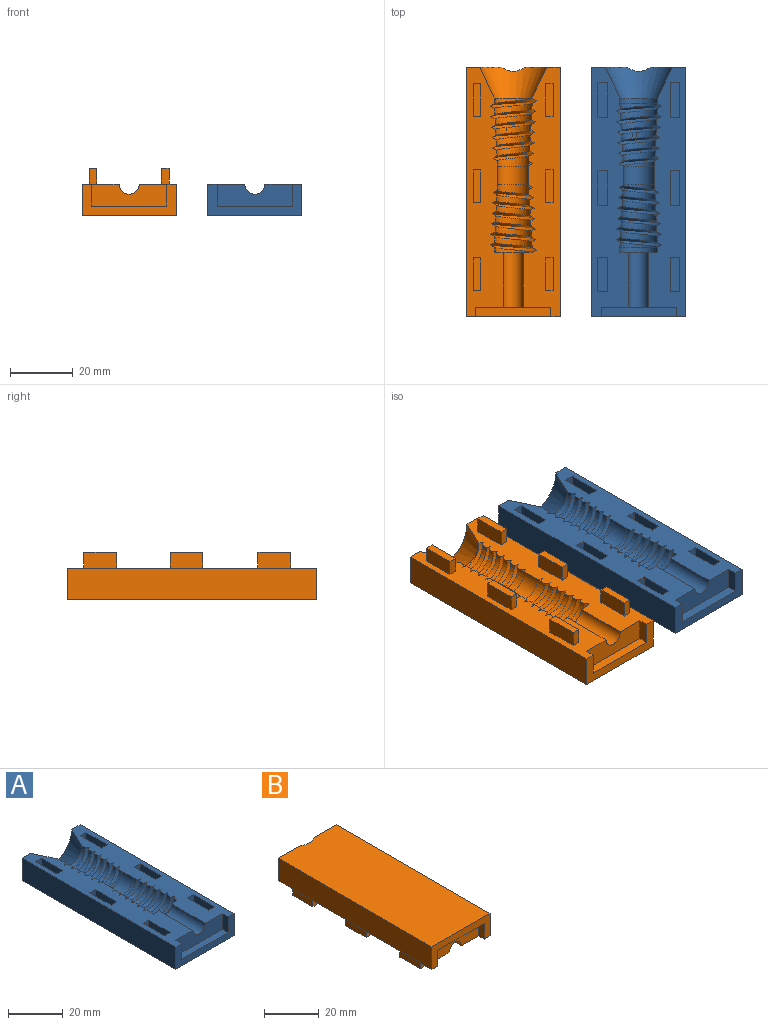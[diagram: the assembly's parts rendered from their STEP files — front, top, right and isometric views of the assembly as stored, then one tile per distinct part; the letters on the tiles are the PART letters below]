
ASSEMBLY  parts=2 mates=3
PART A: 86 faces, bbox 33x82.5x17.5 mm
  f0: plane 79.5x11.8mm, normal (0,0,1), area 638.4mm2, adj f3,f4,f5,f6,f7,f8,f9,f10
  f1: plane 24x3mm, normal (0,0,1), area 72mm2, adj f47,f48,f49,f52
  f2: plane 82.5x32.99mm, normal (0,0,-1), area 2378.5mm2, adj f3,f47,f50,f51,f53,f54
  f3: cone r=5.97mm half-angle=25deg, axis (0,1,0), area 284.2mm2, adj f0,f2,f26,f53,f54,f55
  f4: bspline ~12.74x10mm, area 25.5mm2, adj f0,f5,f21,f26
  f5: bspline ~12.74x10mm, area 26.9mm2, adj f0,f4,f22,f26
  f6: bspline ~13.19x9.88mm, area 26.3mm2, adj f0,f7,f20,f26
  f7: bspline ~13.19x9.88mm, area 27.7mm2, adj f0,f6,f21,f26
  f8: bspline ~13.54x10.18mm, area 27mm2, adj f0,f9,f19,f26
  f9: bspline ~13.54x10.18mm, area 28.5mm2, adj f0,f8,f20,f26
  f10: bspline ~13.83x10.84mm, area 27.8mm2, adj f0,f11,f18,f26
  f11: bspline ~13.83x10.84mm, area 29.4mm2, adj f0,f10,f19,f26
  f12: bspline ~14.2x9.54mm, area 28.6mm2, adj f0,f13,f17,f26
  f13: bspline ~14.2x9.54mm, area 30.2mm2, adj f0,f12,f18,f26
  f14: bspline ~14.59x9.33mm, area 29.4mm2, adj f0,f15,f16,f26
  f15: bspline ~14.59x9.33mm, area 31mm2, adj f0,f14,f17,f26
  f16: cone r=5mm half-angle=3deg, axis (0,1,0), area 19.8mm2, adj f0,f14,f26,f55
  f17: cone r=5mm half-angle=3deg, axis (0,1,0), area 34.7mm2, adj f0,f12,f15,f26
  f18: cone r=5mm half-angle=3deg, axis (0,1,0), area 33.6mm2, adj f0,f10,f13,f26
  f19: cone r=5mm half-angle=3deg, axis (0,1,0), area 32.6mm2, adj f0,f8,f11,f26
  f20: cone r=5mm half-angle=3deg, axis (0,1,0), area 31.6mm2, adj f0,f6,f9,f26
  f21: cone r=5mm half-angle=3deg, axis (0,1,0), area 30.5mm2, adj f0,f4,f7,f26
  f22: cone r=5mm half-angle=3deg, axis (0,1,0), area 13.2mm2, adj f0,f5,f46
  f23: cylinder r=3.2mm len=17.5mm, axis (0,1,0), area 175.9mm2, adj f0,f25,f26,f52
  f24: cylinder r=6.05mm len=12.1mm, axis (0,1,0), area 28.5mm2, adj f0,f25,f26,f45
  f25: plane 12.1x6.05mm, normal (0,1,0), area 41.4mm2, adj f0,f23,f24,f26
  f26: plane 79.5x11.8mm, normal (0,0,1), area 638.3mm2, adj f3,f4,f5,f6,f7,f8,f9,f10
  f27: bspline ~14.59x9.33mm, area 31mm2, adj f0,f26,f28,f44
  f28: bspline ~14.59x9.33mm, area 29.4mm2, adj f0,f26,f27,f45
  f29: bspline ~14.2x9.54mm, area 30.2mm2, adj f0,f26,f30,f43
  f30: bspline ~14.2x9.54mm, area 28.6mm2, adj f0,f26,f29,f44
  f31: bspline ~13.83x10.84mm, area 29.4mm2, adj f0,f26,f32,f42
  f32: bspline ~13.83x10.84mm, area 27.8mm2, adj f0,f26,f31,f43
  f33: bspline ~13.54x10.18mm, area 28.5mm2, adj f0,f26,f34,f41
  f34: bspline ~13.54x10.18mm, area 27mm2, adj f0,f26,f33,f42
  f35: bspline ~13.19x9.88mm, area 27.7mm2, adj f0,f26,f36,f40
  f36: bspline ~13.19x9.88mm, area 26.3mm2, adj f0,f26,f35,f41
  f37: bspline ~12.74x10mm, area 26.9mm2, adj f0,f26,f38,f39
  f38: bspline ~12.74x10mm, area 25.5mm2, adj f0,f26,f37,f40
  f39: cone r=5mm half-angle=3deg, axis (0,-1,0), area 13.2mm2, adj f0,f37,f46
  f40: cone r=5mm half-angle=3deg, axis (0,-1,0), area 30.5mm2, adj f0,f26,f35,f38
  f41: cone r=5mm half-angle=3deg, axis (0,-1,0), area 31.6mm2, adj f0,f26,f33,f36
  f42: cone r=5mm half-angle=3deg, axis (0,-1,0), area 32.6mm2, adj f0,f26,f31,f34
  f43: cone r=5mm half-angle=3deg, axis (0,-1,0), area 33.6mm2, adj f0,f26,f29,f32
  f44: cone r=5mm half-angle=3deg, axis (0,-1,0), area 34.7mm2, adj f0,f26,f27,f30
  f45: cone r=5mm half-angle=3deg, axis (0,-1,0), area 19.8mm2, adj f0,f24,f26,f28
  f46: cylinder r=5mm len=10mm, axis (0,1,0), area 94.2mm2, adj f0,f22,f26,f39
  f47: plane 30x10mm, normal (0,-1,0), area 132mm2, adj f0,f1,f2,f26,f48,f49,f50,f51
  f48: plane 7x3mm, normal (-1,0,0), area 21mm2, adj f0,f1,f47,f52
  f49: plane 7x3mm, normal (1,0,0), area 21mm2, adj f1,f26,f47,f52
  f50: plane 79.5x10mm, normal (1,0,0), area 795mm2, adj f0,f2,f47,f54
  f51: plane 79.5x10mm, normal (-1,0,0), area 795mm2, adj f2,f26,f47,f53
  f52: plane 24x7mm, normal (0,-1,0), area 151.9mm2, adj f0,f1,f23,f26,f48,f49
  f53: plane 11.39x10mm, normal (0,1,0), area 62.8mm2, adj f2,f3,f26,f51
  f54: plane 11.39x10mm, normal (0,1,0), area 62.8mm2, adj f0,f2,f3,f50
  f55: cylinder r=6.05mm len=12.1mm, axis (0,-1,0), area 31.7mm2, adj f0,f3,f16,f26
  f56: plane 11x7mm, normal (-1,0,0), area 77mm2, adj f0,f57,f59,f60
  f57: plane 7x3mm, normal (0,-1,0), area 21mm2, adj f0,f56,f58,f60
  f58: plane 11x7mm, normal (1,0,0), area 77mm2, adj f0,f57,f59,f60
  f59: plane 7x3mm, normal (0,1,0), area 21mm2, adj f0,f56,f58,f60
  f60: plane 11x3mm, normal (0,0,1), area 33mm2, adj f56,f57,f58,f59
  f61: plane 11x7mm, normal (-1,0,0), area 77mm2, adj f0,f62,f64,f65
  f62: plane 7x3mm, normal (0,-1,0), area 21mm2, adj f0,f61,f63,f65
  f63: plane 11x7mm, normal (1,0,0), area 77mm2, adj f0,f62,f64,f65
  f64: plane 7x3mm, normal (0,1,0), area 21mm2, adj f0,f61,f63,f65
  f65: plane 11x3mm, normal (0,0,1), area 33mm2, adj f61,f62,f63,f64
  f66: plane 7x3mm, normal (0,-1,0), area 21mm2, adj f0,f67,f69,f70
  f67: plane 11x7mm, normal (1,0,0), area 77mm2, adj f0,f66,f68,f70
  f68: plane 7x3mm, normal (0,1,0), area 21mm2, adj f0,f67,f69,f70
  f69: plane 11x7mm, normal (-1,0,0), area 77mm2, adj f0,f66,f68,f70
  f70: plane 11x3mm, normal (0,0,1), area 33mm2, adj f66,f67,f68,f69
  f71: plane 11x7mm, normal (1,0,0), area 77mm2, adj f26,f72,f74,f75
  f72: plane 7x3mm, normal (0,1,0), area 21mm2, adj f26,f71,f73,f75
  f73: plane 11x7mm, normal (-1,0,0), area 77mm2, adj f26,f72,f74,f75
  f74: plane 7x3mm, normal (0,-1,0), area 21mm2, adj f26,f71,f73,f75
  f75: plane 11x3mm, normal (0,0,1), area 33mm2, adj f71,f72,f73,f74
  f76: plane 11x7mm, normal (1,0,0), area 77mm2, adj f26,f77,f79,f80
  f77: plane 7x3mm, normal (0,1,0), area 21mm2, adj f26,f76,f78,f80
  f78: plane 11x7mm, normal (-1,0,0), area 77mm2, adj f26,f77,f79,f80
  f79: plane 7x3mm, normal (0,-1,0), area 21mm2, adj f26,f76,f78,f80
  f80: plane 11x3mm, normal (0,0,1), area 33mm2, adj f76,f77,f78,f79
  f81: plane 7x3mm, normal (0,-1,0), area 21mm2, adj f26,f82,f84,f85
  f82: plane 11x7mm, normal (1,0,0), area 77mm2, adj f26,f81,f83,f85
  f83: plane 7x3mm, normal (0,1,0), area 21mm2, adj f26,f82,f84,f85
  f84: plane 11x7mm, normal (-1,0,0), area 77mm2, adj f26,f81,f83,f85
  f85: plane 11x3mm, normal (0,0,1), area 33mm2, adj f81,f82,f83,f84
PART B: 97 faces, bbox 30x79.5x17.9 mm
  f0: plane 79.5x11.8mm, normal (0,0,-1), area 658.6mm2, adj f1,f3,f4,f5,f6,f8,f9,f10
  f1: plane 5x2.5mm, normal (0,1,0), area 12.5mm2, adj f0,f2,f3,f5
  f2: plane 10.5x2.5mm, normal (0,0,-1), area 26.2mm2, adj f1,f3,f4,f5
  f3: plane 10.5x5mm, normal (1,0,0), area 52.5mm2, adj f0,f1,f2,f4
  f4: plane 5x2.5mm, normal (0,-1,0), area 12.5mm2, adj f0,f2,f3,f5
  f5: plane 10.5x5mm, normal (-1,0,0), area 52.5mm2, adj f0,f1,f2,f4
  f6: plane 5x2.5mm, normal (0,-1,0), area 12.5mm2, adj f0,f7,f8,f10
  f7: plane 10.5x2.5mm, normal (0,0,-1), area 26.2mm2, adj f6,f8,f9,f10
  f8: plane 10.5x5mm, normal (-1,0,0), area 52.5mm2, adj f0,f6,f7,f9
  f9: plane 5x2.5mm, normal (0,1,0), area 12.5mm2, adj f0,f7,f8,f10
  f10: plane 10.5x5mm, normal (1,0,0), area 52.5mm2, adj f0,f6,f7,f9
  f11: bspline ~13.68x9.07mm, area 27.4mm2, adj f0,f12,f42,f91
  f12: plane 79.5x11.8mm, normal (0,0,-1), area 656.6mm2, adj f11,f13,f16,f18,f19,f21,f23,f24
  f13: extruded ~11.73x6mm, area 1.4mm2, adj f12,f14,f62
  f14: extruded ~11.73x6mm, area 12.7mm2, adj f13,f15,f65
  f15: extruded ~1.67x0.5mm, area 0.8mm2, adj f14,f62,f63,f65
  f16: plane 11.39x10mm, normal (0,1,0), area 62.8mm2, adj f12,f17,f18,f62
  f17: plane 79.51x30mm, normal (0,0,1), area 2378.5mm2, adj f16,f18,f59,f60,f61,f62
  f18: plane 79.5x10mm, normal (-1,0,0), area 795mm2, adj f12,f16,f17,f59
  f19: plane 7x3mm, normal (1,0,0), area 21mm2, adj f12,f20,f57,f59
  f20: plane 24x3mm, normal (0,0,-1), area 72mm2, adj f19,f57,f58,f59
  f21: bspline ~19.49x14.59mm, area -305.3mm2, adj f12,f22,f23,f84
  f22: plane 1.46x1.3mm, normal (0,0,-1), area 0.9mm2, adj f21,f23,f84
  f23: bspline ~4.54x2.68mm, area 0mm2, adj f12,f21,f22
  f24: bspline ~4.54x2.68mm, area 0mm2, adj f12,f25,f26
  f25: plane 1.46x1.3mm, normal (0,0,-1), area 0.9mm2, adj f24,f26,f82
  f26: bspline ~19.49x14.59mm, area -305.3mm2, adj f12,f24,f25,f82
  f27: plane 10.5x5mm, normal (1,0,0), area 52.5mm2, adj f12,f28,f29,f31
  f28: plane 10.5x2.5mm, normal (0,0,-1), area 26.2mm2, adj f27,f29,f30,f31
  f29: plane 5x2.5mm, normal (0,-1,0), area 12.5mm2, adj f12,f27,f28,f30
  f30: plane 10.5x5mm, normal (-1,0,0), area 52.5mm2, adj f12,f28,f29,f31
  f31: plane 5x2.5mm, normal (0,1,0), area 12.5mm2, adj f12,f27,f28,f30
  f32: plane 10.5x5mm, normal (-1,0,0), area 52.5mm2, adj f12,f33,f34,f36
  f33: plane 10.5x2.5mm, normal (0,0,-1), area 26.2mm2, adj f32,f34,f35,f36
  f34: plane 5x2.5mm, normal (0,1,0), area 12.5mm2, adj f12,f32,f33,f35
  f35: plane 10.5x5mm, normal (1,0,0), area 52.5mm2, adj f12,f33,f34,f36
  f36: plane 5x2.5mm, normal (0,-1,0), area 12.5mm2, adj f12,f32,f33,f35
  f37: plane 10.5x5mm, normal (-1,0,0), area 52.5mm2, adj f12,f38,f39,f41
  f38: plane 10.5x2.5mm, normal (0,0,-1), area 26.2mm2, adj f37,f39,f40,f41
  f39: plane 5x2.5mm, normal (0,1,0), area 12.5mm2, adj f12,f37,f38,f40
  f40: plane 10.5x5mm, normal (1,0,0), area 52.5mm2, adj f12,f38,f39,f41
  f41: plane 5x2.5mm, normal (0,-1,0), area 12.5mm2, adj f12,f37,f38,f40
  f42: cone r=5mm half-angle=3deg, axis (0,-1,0), area 33.1mm2, adj f0,f11,f12,f43
  f43: bspline ~14x11.11mm, area 29.8mm2, adj f0,f12,f42,f44
  f44: bspline ~14x11.11mm, area 28.2mm2, adj f0,f12,f43,f45
  f45: cone r=5mm half-angle=3deg, axis (0,-1,0), area 34.1mm2, adj f0,f12,f44,f46
  f46: bspline ~14.42x10.98mm, area 30.6mm2, adj f0,f12,f45,f47
  f47: bspline ~14.42x10.98mm, area 29mm2, adj f0,f12,f46,f48
  f48: cone r=5mm half-angle=3deg, axis (0,-1,0), area 35.2mm2, adj f0,f12,f47,f49
  f49: bspline ~14.69x10.93mm, area 31.4mm2, adj f0,f12,f48,f50
  f50: bspline ~14.61x7.3mm, area 31.2mm2, adj f0,f12,f49,f51,f52,f53
  f51: extruded ~1.5x0.5mm, area 0.8mm2, adj f50,f52,f54,f55
  f52: extruded ~11.73x6mm, area 12.7mm2, adj f50,f51,f55
  f53: cone r=5mm half-angle=3deg, axis (0,-1,0), area 0.3mm2, adj f0,f50,f54
  f54: cylinder r=6.05mm len=2.34mm, axis (0,1,0), area 3.6mm2, adj f0,f51,f53,f55
  f55: plane 12.11x6.05mm, normal (0,1,0), area 40.7mm2, adj f0,f12,f51,f52,f54,f56
  f56: cylinder r=3.2mm len=17.5mm, axis (0,1,0), area 175.9mm2, adj f0,f12,f55,f57
  f57: plane 24x7mm, normal (0,-1,0), area 151.9mm2, adj f0,f12,f19,f20,f56,f58
  f58: plane 7x3mm, normal (-1,0,0), area 21mm2, adj f0,f20,f57,f59
  f59: plane 30x10mm, normal (0,-1,0), area 132mm2, adj f0,f12,f17,f18,f19,f20,f58,f60
  f60: plane 79.5x10mm, normal (1,0,0), area 795mm2, adj f0,f17,f59,f61
  f61: plane 11.39x10mm, normal (0,1,0), area 62.8mm2, adj f0,f17,f60,f62
  f62: cone r=5.97mm half-angle=25deg, axis (0,1,0), area 278.5mm2, adj f0,f12,f13,f15,f16,f17,f61,f63
  f63: cylinder r=6.05mm len=2.34mm, axis (0,-1,0), area 4mm2, adj f0,f15,f62,f64
  f64: cone r=5mm half-angle=3deg, axis (0,1,0), area 0.3mm2, adj f0,f63,f65
  f65: bspline ~14.61x7.3mm, area 31.2mm2, adj f0,f12,f14,f15,f64,f66
  f66: bspline ~14.69x10.93mm, area 31.4mm2, adj f0,f12,f65,f67
  f67: cone r=5mm half-angle=3deg, axis (0,1,0), area 35.2mm2, adj f0,f12,f66,f68
  f68: bspline ~14.42x10.98mm, area 29mm2, adj f0,f12,f67,f69
  f69: bspline ~14.42x10.98mm, area 30.6mm2, adj f0,f12,f68,f70
  f70: cone r=5mm half-angle=3deg, axis (0,1,0), area 34.1mm2, adj f0,f12,f69,f71
  f71: bspline ~14x11.11mm, area 28.2mm2, adj f0,f12,f70,f72
  f72: bspline ~14x11.11mm, area 29.8mm2, adj f0,f12,f71,f73
  f73: cone r=5mm half-angle=3deg, axis (0,1,0), area 33.1mm2, adj f0,f12,f72,f74
  f74: bspline ~13.68x9.07mm, area 27.4mm2, adj f0,f12,f73,f75
  f75: bspline ~13.68x9.07mm, area 29mm2, adj f0,f12,f74,f76
  f76: cone r=5mm half-angle=3deg, axis (0,1,0), area 32.1mm2, adj f0,f12,f75,f77
  f77: bspline ~13.36x8.43mm, area 26.7mm2, adj f0,f12,f76,f78
  f78: bspline ~13.36x8.43mm, area 28.1mm2, adj f0,f12,f77,f79
  f79: cone r=5mm half-angle=3deg, axis (0,1,0), area 31mm2, adj f0,f12,f78,f80
  f80: bspline ~12.99x8.56mm, area 25.9mm2, adj f0,f12,f79,f81
  f81: bspline ~12.99x8.56mm, area 27.3mm2, adj f0,f12,f80,f82
  f82: cone r=5mm half-angle=3deg, axis (0,1,0), area 1485.7mm2, adj f0,f12,f25,f26,f81,f83
  f83: cylinder r=5mm len=10mm, axis (0,1,0), area 94.2mm2, adj f0,f12,f82,f84
  f84: cone r=5mm half-angle=3deg, axis (0,-1,0), area 1487.6mm2, adj f0,f12,f21,f22,f83,f85
  f85: bspline ~12.99x8.56mm, area 27.3mm2, adj f0,f12,f84,f86
  f86: bspline ~12.99x8.56mm, area 25.9mm2, adj f0,f12,f85,f87
  f87: cone r=5mm half-angle=3deg, axis (0,-1,0), area 31mm2, adj f0,f12,f86,f88
  f88: bspline ~13.21x6.6mm, area 28.1mm2, adj f0,f12,f87,f89
  f89: bspline ~13.36x8.43mm, area 26.7mm2, adj f0,f12,f88,f90
  f90: cone r=5mm half-angle=3deg, axis (0,-1,0), area 32.1mm2, adj f0,f12,f89,f91
  f91: bspline ~13.68x9.07mm, area 29mm2, adj f0,f11,f12,f90
  f92: plane 5x2.5mm, normal (0,1,0), area 12.5mm2, adj f0,f93,f94,f96
  f93: plane 10.5x2.5mm, normal (0,0,-1), area 26.2mm2, adj f92,f94,f95,f96
  f94: plane 10.5x5mm, normal (1,0,0), area 52.5mm2, adj f0,f92,f93,f95
  f95: plane 5x2.5mm, normal (0,-1,0), area 12.5mm2, adj f0,f93,f94,f96
  f96: plane 10.5x5mm, normal (-1,0,0), area 52.5mm2, adj f0,f92,f93,f95
PLACE A t=(-16.9,-10.86,21.13)mm
PLACE B rot(axis=(0,1,0),180deg) t=(-56.9,-10.86,21.13)mm
MATE planar B.f17 <-> A.f2  axis (0,0,-1) through (-56.9,-16.22,11.13)mm
MATE parallel B.f18 <-> A.f51  axis (1,0,0) through (-41.9,-55.86,16.13)mm
MATE planar B.f59 <-> A.f47  axis (0,-1,0) through (-44.9,-55.86,14.13)mm
